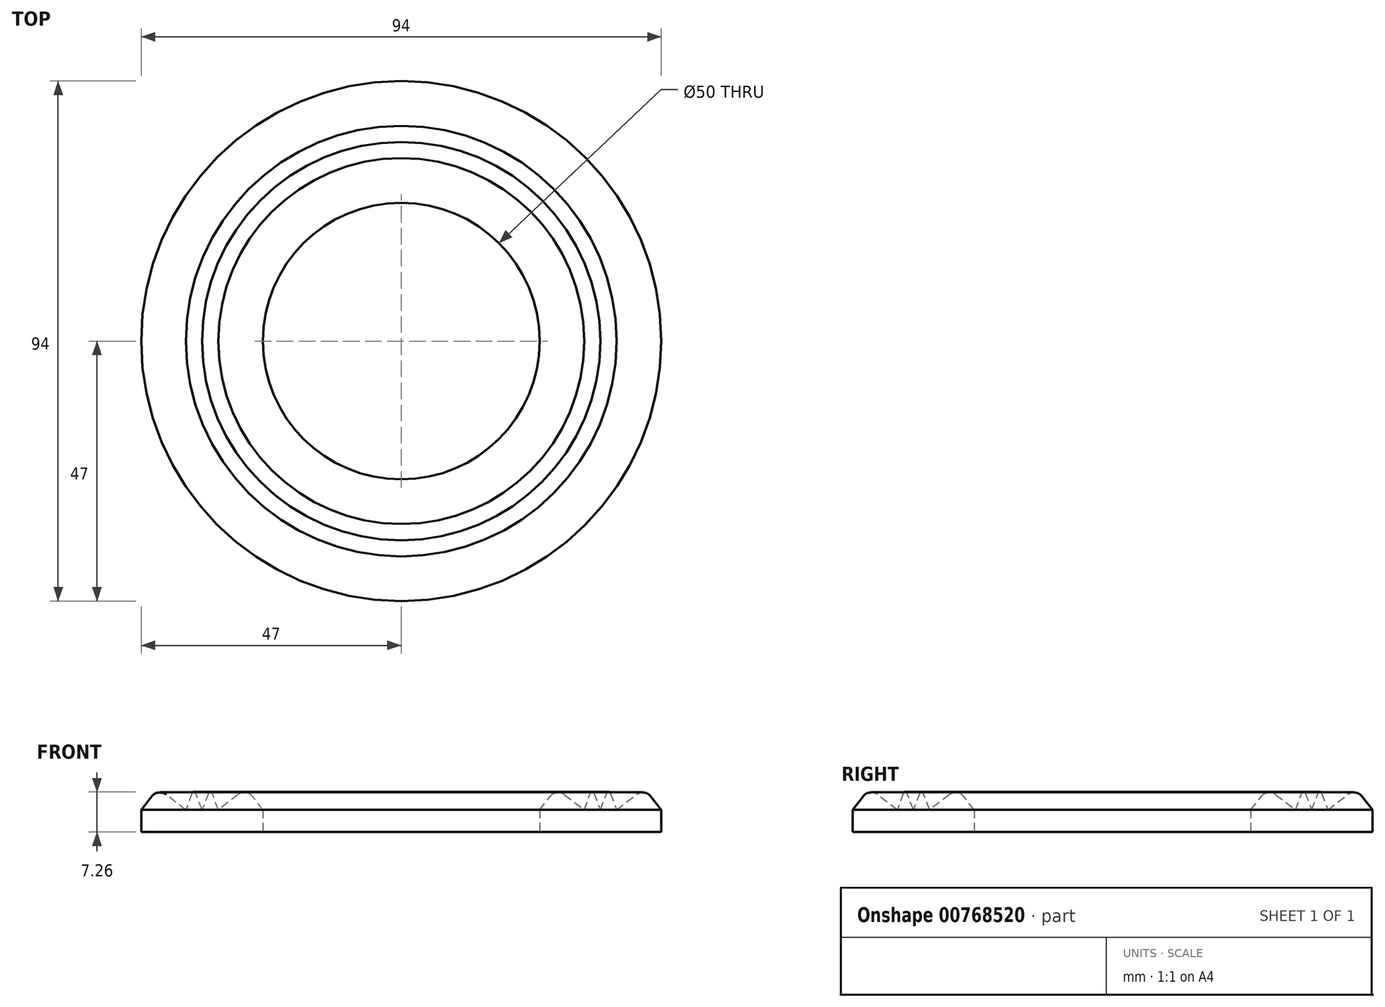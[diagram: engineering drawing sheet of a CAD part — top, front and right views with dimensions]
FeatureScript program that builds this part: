
annotation { "Feature Type Name" : "Feature", "Feature Type Description" : "" }
export const myFeature = defineFeature(function(context is Context, id is Id, definition is map)
    precondition{}
    {
        {
            var Q0;
            Q0=qCreatedBy(makeId("Front.planeOp"),FACE);
            var sketch = newSketch(context, id + "F0", { "sketchPlane" : qUnion([Q0])});
            skLineSegment(sketch, "E0", {"start": v(-25, 0) * mm, "end": v(-47, 0) * mm});
            skLineSegment(sketch, "E1", {"start": v(-47, 0) * mm, "end": v(-47, 4) * mm});
            skLineSegment(sketch, "E2", {"start": v(-33.07, 4) * mm, "end": v(-33.05, 4) * mm});
            skLineSegment(sketch, "E3", {"start": v(-25, 4) * mm, "end": v(-25, 0) * mm});
            skLineSegment(sketch, "E4", {"start": v(0, 0) * mm, "end": v(0, 4) * mm});
            skLineSegment(sketch, "E5", {"start": v(-47, 4) * mm, "end": v(-45.1, 6.45) * mm});
            skLineSegment(sketch, "E6", {"start": v(-42.5, 6.78) * mm, "end": v(-38.93, 4) * mm});
            skLineSegment(sketch, "E7", {"start": v(-33.07, 3.98) * mm, "end": v(-33.02, 4.04) * mm});
            skLineSegment(sketch, "E8", {"start": v(-25.02, 4) * mm, "end": v(-25, 3.98) * mm});
            skPoint(sketch, "E9.start.orphan", {"position": v(-47, 2) * mm});
            skLineSegment(sketch, "E10.MirrorCS", {"start": v(-29.5, 6.78) * mm, "end": v(-33.07, 4) * mm});
            skLineSegment(sketch, "E11.MirrorCS", {"start": v(-25, 4) * mm, "end": v(-26.9, 6.45) * mm});
            skLineSegment(sketch, "E12", {"start": v(-38.93, 4) * mm, "end": v(-37.82, 7.03) * mm});
            skLineSegment(sketch, "E13", {"start": v(-37.17, 7.04) * mm, "end": v(-36, 4) * mm});
            skLineSegment(sketch, "E14.MirrorCS", {"start": v(-34.83, 7.04) * mm, "end": v(-36, 4) * mm});
            skLineSegment(sketch, "E15.MirrorCS", {"start": v(-33.07, 4) * mm, "end": v(-34.18, 7.03) * mm});
            skPoint(sketch, "E16.end.orphan", {"position": v(-36, 0) * mm});
            skLineSegment(sketch, "E17.trimOffspring", {"start": v(-25.02, 4) * mm, "end": v(-25, 4) * mm});
            skPoint(sketch, "E18.visualSharp", {"position": v(-43.96, 7.91) * mm});
            skArc(sketch, "E18.filletArc", {"start": v(-42.5, 6.78) * mm, "mid": v(-43.86, 7.15) * mm, "end": v(-45.1, 6.45) * mm});
            skPoint(sketch, "E19.visualSharp", {"position": v(-28.04, 7.91) * mm});
            skArc(sketch, "E19.filletArc", {"start": v(-26.9, 6.45) * mm, "mid": v(-28.14, 7.15) * mm, "end": v(-29.5, 6.78) * mm});
            skPoint(sketch, "E20.visualSharp", {"position": v(-37.5, 7.91) * mm});
            skArc(sketch, "E20.filletArc", {"start": v(-37.17, 7.04) * mm, "mid": v(-37.5, 7.26) * mm, "end": v(-37.82, 7.03) * mm});
            skArc(sketch, "E21.MirrorCS", {"start": v(-34.83, 7.04) * mm, "mid": v(-34.5, 7.26) * mm, "end": v(-34.18, 7.03) * mm});
            skSolve(sketch);
        }
        {
            var Q0;
            Q0=qSketchRegion(id+"F0",true);
            var Q1;
            Q1=sQuery(id+"F0.wireOp",EDGE,"E4");
            revolve(context, id + "F1", {"surfaceOperationType" : NewSurfaceOperationType.NEW, "entities" : qUnion([Q0]), "axis" : qUnion([Q1]), "revolveType" : RevolveType.FULL});
        }
    });
